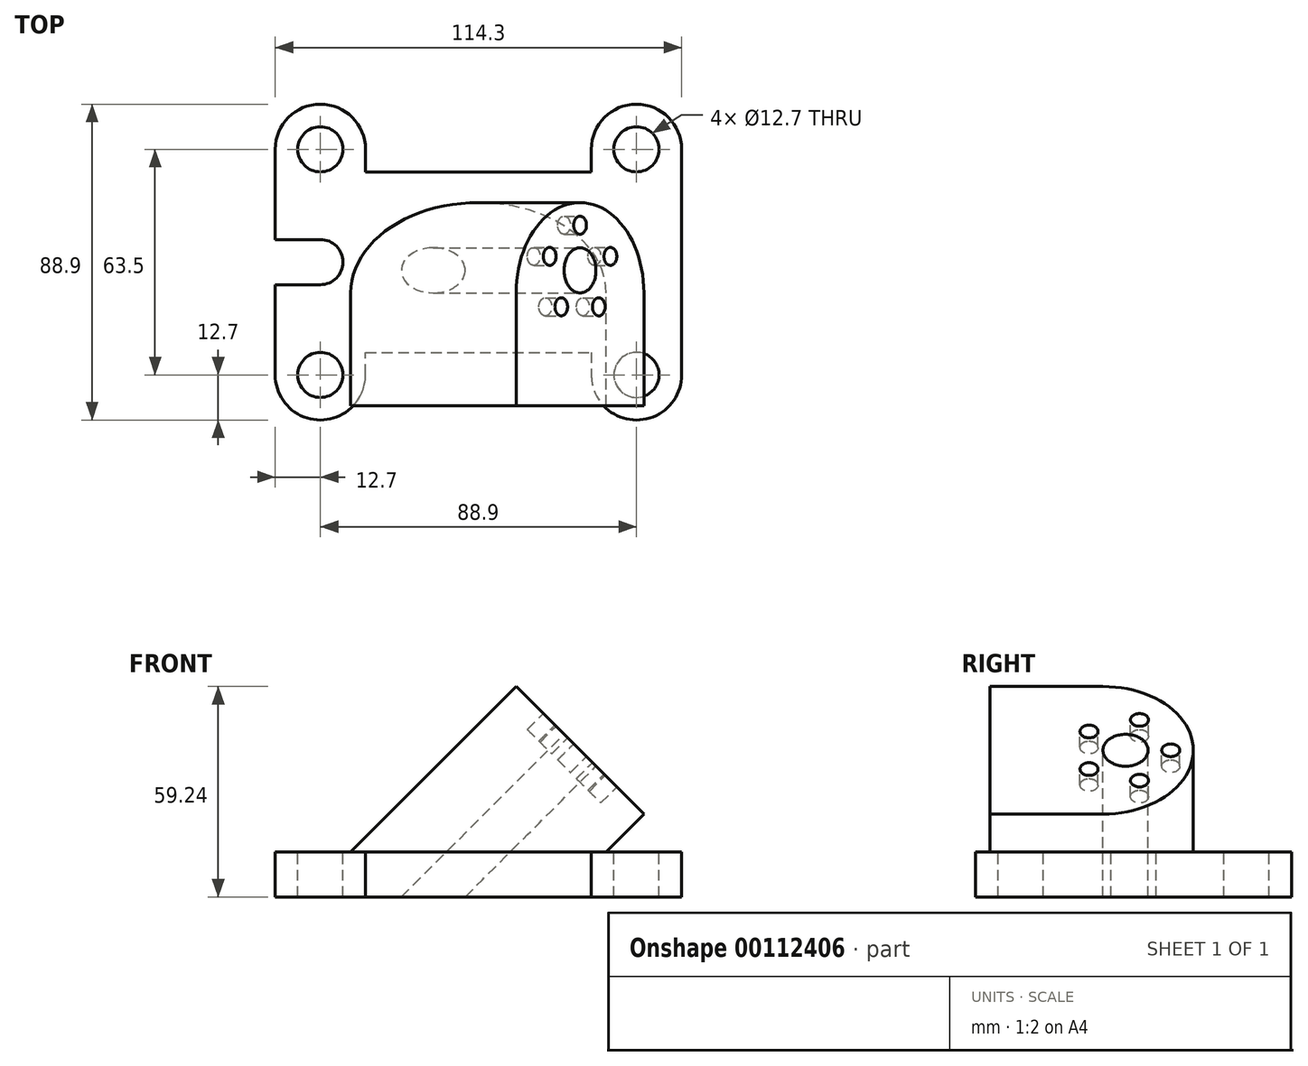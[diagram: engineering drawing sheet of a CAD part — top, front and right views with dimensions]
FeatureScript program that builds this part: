
annotation { "Feature Type Name" : "Feature", "Feature Type Description" : "" }
export const myFeature = defineFeature(function(context is Context, id is Id, definition is map)
    precondition{}
    {
        {
            var Q0;
            Q0=qCreatedBy(makeId("Top.planeOp"),FACE);
            var sketch = newSketch(context, id + "F0", { "sketchPlane" : qUnion([Q0])});
            skLineSegment(sketch, "E0", {"start": v(-83.08, 31.75) * mm, "end": v(125, 31.75) * mm, "construction": true});
            skLineSegment(sketch, "E1", {"start": v(-44.45, 91.15) * mm, "end": v(-44.45, -70.29) * mm, "construction": true});
            skLineSegment(sketch, "E2", {"start": v(-84.05, -31.75) * mm, "end": v(132.33, -31.75) * mm, "construction": true});
            skLineSegment(sketch, "E3", {"start": v(44.45, 86.02) * mm, "end": v(44.45, -64.43) * mm, "construction": true});
            skLineSegment(sketch, "E4", {"start": v(-86.73, 0) * mm, "end": v(130.54, 0) * mm, "construction": true});
            skSolve(sketch);
        }
        {
            var Q0;
            Q0=qCreatedBy(makeId("Top.planeOp"),FACE);
            var sketch = newSketch(context, id + "F1", { "sketchPlane" : qUnion([Q0])});
            skLineSegment(sketch, "E5", {"start": v(-57.15, 31.75) * mm, "end": v(-57.15, 6.35) * mm});
            skLineSegment(sketch, "E6", {"start": v(-31.75, -31.75) * mm, "end": v(-31.75, -25.4) * mm});
            skLineSegment(sketch, "E7", {"start": v(-31.75, -25.4) * mm, "end": v(31.75, -25.4) * mm});
            skLineSegment(sketch, "E8", {"start": v(31.75, -25.4) * mm, "end": v(31.75, -31.75) * mm});
            skLineSegment(sketch, "E9", {"start": v(57.15, -31.75) * mm, "end": v(57.15, 31.75) * mm});
            skCircle(sketch, "E10", {"center": v(-44.45, 31.75) * mm, "radius": 6.35 * mm});
            skCircle(sketch, "E11", {"center": v(-44.45, -31.75) * mm, "radius": 6.35 * mm});
            skCircle(sketch, "E12", {"center": v(44.45, -31.75) * mm, "radius": 6.35 * mm});
            skCircle(sketch, "E13", {"center": v(44.45, 31.75) * mm, "radius": 6.35 * mm});
            skArc(sketch, "E14", {"start": v(-31.75, 31.75) * mm, "mid": v(-44.45, 44.45) * mm, "end": v(-57.15, 31.75) * mm});
            skArc(sketch, "E15", {"start": v(-57.15, -31.75) * mm, "mid": v(-44.45, -44.45) * mm, "end": v(-31.75, -31.75) * mm});
            skLineSegment(sketch, "E16", {"start": v(-44.45, -44.45) * mm, "end": v(-44.45, 57.86) * mm, "construction": true});
            skLineSegment(sketch, "E17", {"start": v(-31.75, 31.75) * mm, "end": v(-31.75, 25.4) * mm});
            skLineSegment(sketch, "E18", {"start": v(-31.75, 25.4) * mm, "end": v(31.75, 25.4) * mm});
            skLineSegment(sketch, "E19", {"start": v(31.75, 25.4) * mm, "end": v(31.75, 31.75) * mm});
            skArc(sketch, "E20", {"start": v(-44.45, 6.35) * mm, "mid": v(-38.1, 0) * mm, "end": v(-44.45, -6.35) * mm});
            skLineSegment(sketch, "E21", {"start": v(-44.45, 6.35) * mm, "end": v(-57.15, 6.35) * mm});
            skLineSegment(sketch, "E22", {"start": v(-44.45, -6.35) * mm, "end": v(-57.15, -6.35) * mm});
            skLineSegment(sketch, "E23.trimOffspring", {"start": v(-57.15, -6.35) * mm, "end": v(-57.15, -31.75) * mm});
            skArc(sketch, "E24", {"start": v(57.15, 31.75) * mm, "mid": v(44.45, 44.45) * mm, "end": v(31.75, 31.75) * mm});
            skArc(sketch, "E25", {"start": v(31.75, -31.75) * mm, "mid": v(44.45, -44.45) * mm, "end": v(57.15, -31.75) * mm});
            skPoint(sketch, "E26.startSnap0", {"position": v(-38.1, 0) * mm});
            skPoint(sketch, "E26.endSnap0", {"position": v(-38.1, 0) * mm});
            skLineSegment(sketch, "E27", {"start": v(-52.1, 0) * mm, "end": v(90.73, 0) * mm, "construction": true});
            skLineSegment(sketch, "E28", {"start": v(-26.8, -31.75) * mm, "end": v(-66.05, -31.75) * mm, "construction": true});
            skPoint(sketch, "E29", {"position": v(-44.45, 44.45) * mm});
            skLineSegment(sketch, "E30", {"start": v(-72.22, 31.75) * mm, "end": v(-17.6, 31.75) * mm, "construction": true});
            skSolve(sketch);
        }
        {
            var Q0;
            Q0=makeQuery(id+"F1.imprint","IMPRINT",FACE,{"disambiguationData":[TD([[makeQuery(id+"F1.imprint","IMPRINT",EDGE,{"derivedFrom":sQuery(id+"F1.wireOp",EDGE,"E5")}),1.0]])]});
            var Q1;
            Q1=makeQuery(id+"F1.imprint","IMPRINT",FACE,{"disambiguationData":[TD([[makeQuery(id+"F1.imprint","IMPRINT",EDGE,{"derivedFrom":sQuery(id+"F1.wireOp",EDGE,"E11")}),1.0]])]});
            var Q2;
            Q2=makeQuery(id+"F1.imprint","IMPRINT",FACE,{"disambiguationData":[TD([[makeQuery(id+"F1.imprint","IMPRINT",EDGE,{"derivedFrom":sQuery(id+"F1.wireOp",EDGE,"E10")}),1.0]])]});
            var Q3;
            Q3=makeQuery(id+"F1.imprint","IMPRINT",FACE,{"disambiguationData":[TD([[makeQuery(id+"F1.imprint","IMPRINT",EDGE,{"derivedFrom":sQuery(id+"F1.wireOp",EDGE,"E13")}),1.0]])]});
            var Q4;
            Q4=makeQuery(id+"F1.imprint","IMPRINT",FACE,{"disambiguationData":[TD([[makeQuery(id+"F1.imprint","IMPRINT",EDGE,{"derivedFrom":sQuery(id+"F1.wireOp",EDGE,"E12")}),1.0]])]});
            extrude(context, id + "F2", {"entities" : qUnion([Q0, Q1, Q2, Q3, Q4]), "oppositeDirection" : true, "depth" : 12.7 * mm});
        }
        {
            var Q0;
            Q0=makeQuery(id+"F1.imprint","IMPRINT",FACE,{"disambiguationData":[TD([[makeQuery(id+"F1.imprint","IMPRINT",EDGE,{"derivedFrom":sQuery(id+"F1.wireOp",EDGE,"E5")}),1.0]])]});
            var sketch = newSketch(context, id + "F3", { "sketchPlane" : qUnion([Q0])});
            skCircle(sketch, "E31.0", {"center": v(-44.45, -31.75) * mm, "radius": 6.35 * mm});
            skCircle(sketch, "E31.1", {"center": v(-44.45, 31.75) * mm, "radius": 6.35 * mm});
            skCircle(sketch, "E31.2", {"center": v(44.45, 31.75) * mm, "radius": 6.35 * mm});
            skCircle(sketch, "E31.3", {"center": v(44.45, -31.75) * mm, "radius": 6.35 * mm});
            skSolve(sketch);
        }
        {
            var Q0;
            Q0=makeQuery(id+"F1.imprint","IMPRINT",FACE,{"disambiguationData":[TD([[makeQuery(id+"F1.imprint","IMPRINT",EDGE,{"derivedFrom":sQuery(id+"F1.wireOp",EDGE,"E11")}),1.0]])]});
            var Q1;
            Q1=makeQuery(id+"F1.imprint","IMPRINT",FACE,{"disambiguationData":[TD([[makeQuery(id+"F1.imprint","IMPRINT",EDGE,{"derivedFrom":sQuery(id+"F1.wireOp",EDGE,"E10")}),1.0]])]});
            var Q2;
            Q2=makeQuery(id+"F1.imprint","IMPRINT",FACE,{"disambiguationData":[TD([[makeQuery(id+"F1.imprint","IMPRINT",EDGE,{"derivedFrom":sQuery(id+"F1.wireOp",EDGE,"E13")}),1.0]])]});
            var Q3;
            Q3=makeQuery(id+"F1.imprint","IMPRINT",FACE,{"disambiguationData":[TD([[makeQuery(id+"F1.imprint","IMPRINT",EDGE,{"derivedFrom":sQuery(id+"F1.wireOp",EDGE,"E12")}),1.0]])]});
            extrude(context, id + "F4", {"entities" : qUnion([Q0, Q1, Q2, Q3]), "operationType" : NewBodyOperationType.REMOVE, "endBound" : BoundingType.THROUGH_ALL, "oppositeDirection" : true, "depth" : 25.4 * mm});
        }
        {
            var Q0;
            Q0=sQuery(id+"F1.wireOp",EDGE,"E9");
            var Q1;
            Q1=makeQuery(id+"F1.imprint","IMPRINT",FACE,{"disambiguationData":[TD([[makeQuery(id+"F1.imprint","IMPRINT",EDGE,{"derivedFrom":sQuery(id+"F1.wireOp",EDGE,"E5")}),1.0]])]});
            cPlane(context, id + "F5", {"entities" : qUnion([Q0, Q1]), "cplaneType" : CPlaneType.LINE_ANGLE, "offset" : 25.4 * mm, "angle" : 45 * degree, "width" : 152.4 * mm, "height" : 152.4 * mm});
        }
        {
            var Q0;
            Q0=qCreatedBy(id+"F5.planeOp",FACE);
            var sketch = newSketch(context, id + "F6", { "sketchPlane" : qUnion([Q0])});
            skLineSegment(sketch, "E32.0", {"start": v(40.41, 31.75) * mm, "end": v(40.41, -31.75) * mm});
            skLineSegment(sketch, "E33", {"start": v(40.41, 25.4) * mm, "end": v(8.66, 25.4) * mm});
            skArc(sketch, "E34", {"start": v(8.66, 25.4) * mm, "mid": v(-16.74, 0) * mm, "end": v(8.66, -25.4) * mm});
            skLineSegment(sketch, "E35", {"start": v(8.66, -25.4) * mm, "end": v(40.41, -25.4) * mm});
            skSolve(sketch);
        }
        {
            var Q0;
            {var subQ0=sQuery(id+"F6.wireOp",EDGE,"E33");Q0=makeQuery(id+"F6.imprint","IMPRINT",FACE,{"disambiguationData":[TD([[makeQuery(id+"F6.imprint","IMPRINT",EDGE,{"derivedFrom":subQ0}),1.0]])]});}
            var Q1;
            Q1=makeQuery(id+"F2.opExtrude","CAP_FACE",FACE,{"disambiguationData":[OSD([sQuery(id+"F1.wireOp",EDGE,"E5"),sQuery(id+"F1.wireOp",EDGE,"E6"),sQuery(id+"F1.wireOp",EDGE,"E7"),sQuery(id+"F1.wireOp",EDGE,"E8"),sQuery(id+"F1.wireOp",EDGE,"E9"),sQuery(id+"F1.wireOp",EDGE,"E14"),sQuery(id+"F1.wireOp",EDGE,"E15"),sQuery(id+"F1.wireOp",EDGE,"E17"),sQuery(id+"F1.wireOp",EDGE,"E18"),sQuery(id+"F1.wireOp",EDGE,"E19"),sQuery(id+"F1.wireOp",EDGE,"E20"),sQuery(id+"F1.wireOp",EDGE,"E21"),sQuery(id+"F1.wireOp",EDGE,"E22"),sQuery(id+"F1.wireOp",EDGE,"E23.trimOffspring"),sQuery(id+"F1.wireOp",EDGE,"E24"),sQuery(id+"F1.wireOp",EDGE,"E25")])],"isStart":true});
            extrude(context, id + "F7", {"entities" : qUnion([Q0]), "operationType" : NewBodyOperationType.ADD, "endBound" : BoundingType.UP_TO_SURFACE, "endBoundEntityFace" : qUnion([Q1]), "depth" : 25.4 * mm});
        }
        {
            var Q0;
            Q0=qCreatedBy(id+"F5.planeOp",FACE);
            var sketch = newSketch(context, id + "F8", { "sketchPlane" : qUnion([Q0])});
            skCircle(sketch, "E36", {"center": v(12.59, 7.46) * mm, "radius": 2.54 * mm});
            skCircle(sketch, "E37.1.0", {"center": v(12.59, -7.46) * mm, "radius": 2.54 * mm});
            skCircle(sketch, "E37.2.0", {"center": v(-1.61, -12.08) * mm, "radius": 2.54 * mm});
            skCircle(sketch, "E37.3.0", {"center": v(-10.39, 0) * mm, "radius": 2.54 * mm});
            skCircle(sketch, "E37.4.0", {"center": v(-1.61, 12.08) * mm, "radius": 2.54 * mm});
            skPoint(sketch, "E37.center", {"position": v(2.31, 0) * mm});
            skCircle(sketch, "E38", {"center": v(2.31, 0) * mm, "radius": 12.7 * mm, "construction": true});
            skCircle(sketch, "E39", {"center": v(2.31, 0) * mm, "radius": 6.35 * mm});
            skLineSegment(sketch, "E40", {"start": v(2.31, 0) * mm, "end": v(-7.93, 0) * mm, "construction": true});
            skLineSegment(sketch, "E41", {"start": v(2.31, 0) * mm, "end": v(-3.5, -17.86) * mm, "construction": true});
            skLineSegment(sketch, "E42", {"start": v(2.31, 0) * mm, "end": v(14.42, -8.8) * mm, "construction": true});
            skLineSegment(sketch, "E43", {"start": v(2.31, 0) * mm, "end": v(14.84, 9.1) * mm, "construction": true});
            skLineSegment(sketch, "E44", {"start": v(2.31, 0) * mm, "end": v(0, 7.11) * mm, "construction": true});
            skSolve(sketch);
        }
        {
            var Q0;
            {var subQ0=sQuery(id+"F6.wireOp",EDGE,"E33");Q0=makeQuery(id+"F6.imprint","IMPRINT",FACE,{"disambiguationData":[TD([[makeQuery(id+"F6.imprint","IMPRINT",EDGE,{"derivedFrom":subQ0}),1.0]])]});}
            var sketch = newSketch(context, id + "F9", { "sketchPlane" : qUnion([Q0])});
            skCircle(sketch, "E45.0", {"center": v(-10.39, 0) * mm, "radius": 2.54 * mm});
            skCircle(sketch, "E45.1", {"center": v(-1.61, -12.08) * mm, "radius": 2.54 * mm});
            skCircle(sketch, "E45.2", {"center": v(12.59, -7.46) * mm, "radius": 2.54 * mm});
            skCircle(sketch, "E45.3", {"center": v(12.59, 7.46) * mm, "radius": 2.54 * mm});
            skCircle(sketch, "E45.4", {"center": v(-1.61, 12.08) * mm, "radius": 2.54 * mm});
            skCircle(sketch, "E46.0", {"center": v(2.31, 0) * mm, "radius": 6.35 * mm});
            skSolve(sketch);
        }
        {
            var Q0;
            Q0=makeQuery(id+"F8.imprint","IMPRINT",FACE,{"disambiguationData":[TD([[makeQuery(id+"F8.imprint","IMPRINT",EDGE,{"derivedFrom":sQuery(id+"F8.wireOp",EDGE,"E37.3.0")}),1.0]])]});
            var Q1;
            Q1=makeQuery(id+"F8.imprint","IMPRINT",FACE,{"disambiguationData":[TD([[makeQuery(id+"F8.imprint","IMPRINT",EDGE,{"derivedFrom":sQuery(id+"F8.wireOp",EDGE,"E37.2.0")}),1.0]])]});
            var Q2;
            Q2=makeQuery(id+"F8.imprint","IMPRINT",FACE,{"disambiguationData":[TD([[makeQuery(id+"F8.imprint","IMPRINT",EDGE,{"derivedFrom":sQuery(id+"F8.wireOp",EDGE,"E37.1.0")}),1.0]])]});
            var Q3;
            Q3=makeQuery(id+"F8.imprint","IMPRINT",FACE,{"disambiguationData":[TD([[makeQuery(id+"F8.imprint","IMPRINT",EDGE,{"derivedFrom":sQuery(id+"F8.wireOp",EDGE,"E36")}),1.0]])]});
            var Q4;
            Q4=makeQuery(id+"F8.imprint","IMPRINT",FACE,{"disambiguationData":[TD([[makeQuery(id+"F8.imprint","IMPRINT",EDGE,{"derivedFrom":sQuery(id+"F8.wireOp",EDGE,"E37.4.0")}),1.0]])]});
            extrude(context, id + "F10", {"entities" : qUnion([Q0, Q1, Q2, Q3, Q4]), "operationType" : NewBodyOperationType.REMOVE, "depth" : 6.35 * mm});
        }
        {
            var Q0;
            Q0=makeQuery(id+"F9.imprint","IMPRINT",FACE,{"disambiguationData":[TD([[makeQuery(id+"F9.imprint","IMPRINT",EDGE,{"derivedFrom":sQuery(id+"F9.wireOp",EDGE,"E46.0")}),1.0]])]});
            extrude(context, id + "F11", {"entities" : qUnion([Q0]), "operationType" : NewBodyOperationType.REMOVE, "endBound" : BoundingType.THROUGH_ALL, "depth" : 25.4 * mm});
        }
    });
